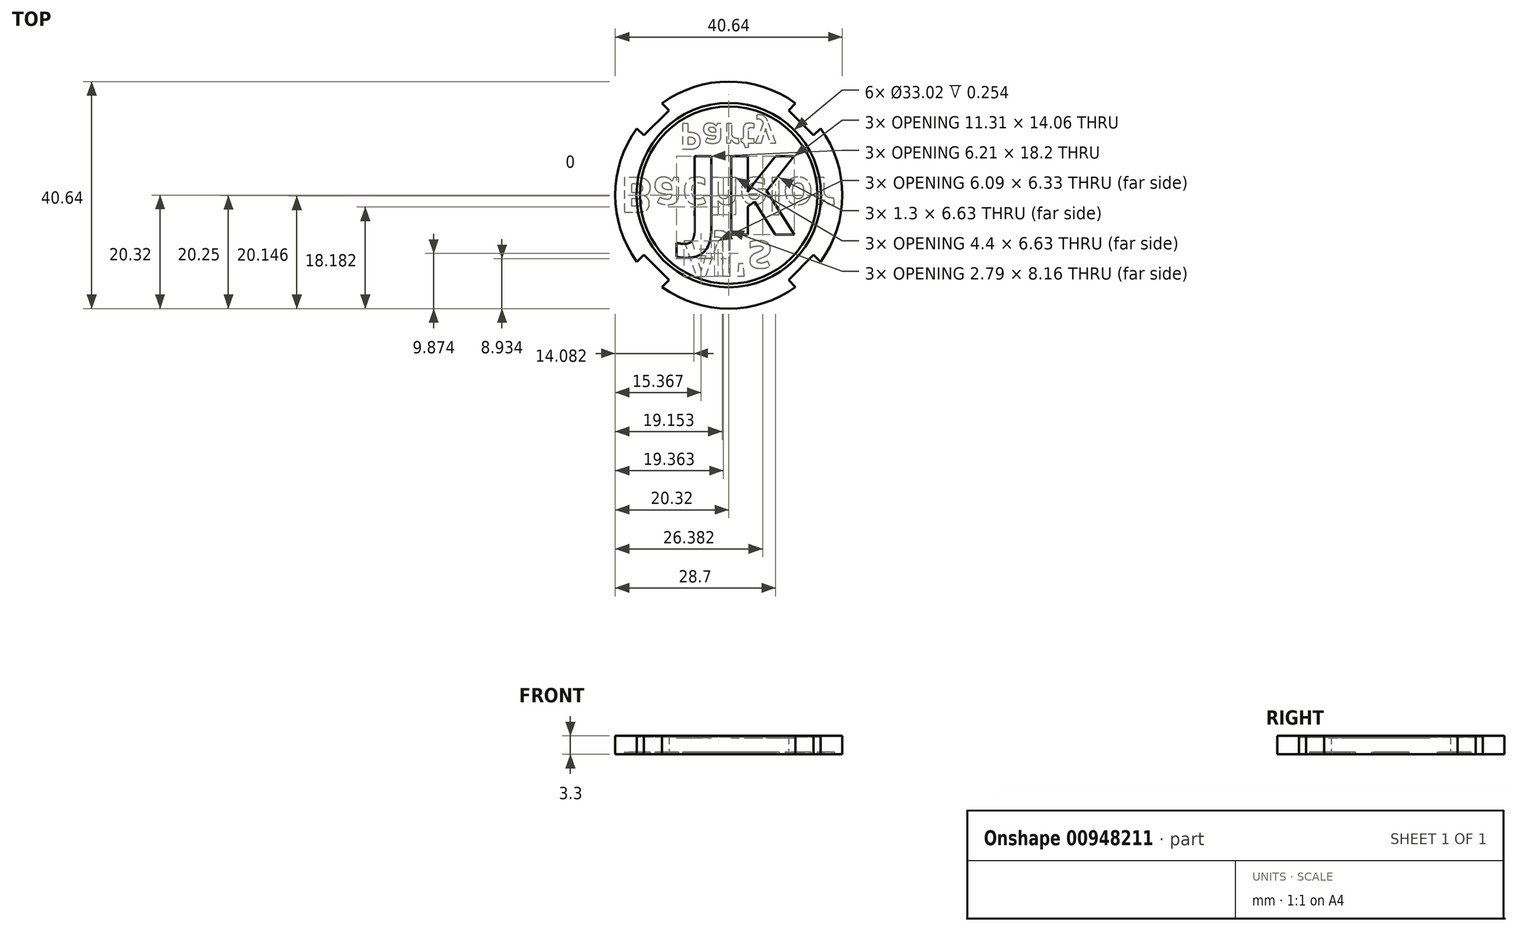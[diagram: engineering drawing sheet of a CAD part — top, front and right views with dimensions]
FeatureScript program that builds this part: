
annotation { "Feature Type Name" : "Feature", "Feature Type Description" : "" }
export const myFeature = defineFeature(function(context is Context, id is Id, definition is map)
    precondition{}
    {
        {
            var Q0;
            Q0=qCreatedBy(makeId("Top.planeOp"),FACE);
            var sketch = newSketch(context, id + "F0", { "sketchPlane" : qUnion([Q0])});
            skCircle(sketch, "E0", {"center": v(0, 0) * mm, "radius": 20.32 * mm});
            skSolve(sketch);
        }
        {
            var Q0;
            Q0=makeQuery(id+"F0.imprint","IMPRINT",FACE,{"disambiguationData":[TD([[makeQuery(id+"F0.imprint","IMPRINT",EDGE,{"derivedFrom":sQuery(id+"F0.wireOp",EDGE,"E0")}),1.0]])]});
            extrude(context, id + "F1", {"entities" : qUnion([Q0]), "depth" : 3.3 * mm, "offsetDistance" : 25.4 * mm});
        }
        {
            var Q0;
            Q0=makeQuery(id+"F1.opExtrude","CAP_FACE",FACE,{"disambiguationData":[OSD([sQuery(id+"F0.wireOp",EDGE,"E0")])],"isStart":true});
            var sketch = newSketch(context, id + "F2", { "sketchPlane" : qUnion([Q0])});
            skText(sketch, "E1", { "text": "Bachelor", "fontName": "OpenSans-Bold.ttf"});
            const initialGuessF2  = {"E1": [-0.01945, -0.00314, 1, 0, 0.00628]};
            skSetInitialGuess(sketch, initialGuessF2);
            skSolve(sketch);
        }
        {
            var Q0;
            Q0=makeQuery(id+"F2.imprint","IMPRINT",FACE,{"disambiguationData":[TD([[makeQuery(id+"F2.imprint","IMPRINT",EDGE,{"derivedFrom":sQuery(id+"F2.wireOp",EDGE,"E1.sketch_text.stroke-0")}),1.0]])]});
            var sketch = newSketch(context, id + "F3", { "sketchPlane" : qUnion([Q0])});
            skText(sketch, "E2", { "text": "AJ\'s", "fontName": "OpenSans-Bold.ttf"});
            const initialGuessF3  = {"E2": [-0.008, 0.00822, 1, 0, 0.00636]};
            skSetInitialGuess(sketch, initialGuessF3);
            skSolve(sketch);
        }
        {
            var Q0;
            Q0=makeQuery(id+"F2.imprint","IMPRINT",FACE,{"disambiguationData":[TD([[makeQuery(id+"F2.imprint","IMPRINT",EDGE,{"derivedFrom":sQuery(id+"F2.wireOp",EDGE,"E1.sketch_text.stroke-0")}),1.0]])]});
            var sketch = newSketch(context, id + "F4", { "sketchPlane" : qUnion([Q0])});
            skText(sketch, "E3", { "text": "Party", "fontName": "OpenSans-Bold.ttf"});
            const initialGuessF4  = {"E3": [-0.00883, -0.01283, 1, 0, 0.00462]};
            skSetInitialGuess(sketch, initialGuessF4);
            skSolve(sketch);
        }
        {
            var Q0;
            Q0=makeQuery(id+"F2.imprint","IMPRINT",FACE,{"disambiguationData":[TD([[makeQuery(id+"F2.imprint","IMPRINT",EDGE,{"derivedFrom":sQuery(id+"F2.wireOp",EDGE,"E1.sketch_text.stroke-0")}),1.0]])]});
            var sketch = newSketch(context, id + "F5", { "sketchPlane" : qUnion([Q0])});
            skLineSegment(sketch, "E4", {"start": v(-14.37, 14.37) * mm, "end": v(14.37, -14.37) * mm, "construction": true});
            skLineSegment(sketch, "E5", {"start": v(-15.18, 10.69) * mm, "end": v(-10.69, 15.18) * mm});
            skLineSegment(sketch, "E6", {"start": v(-10.69, 15.18) * mm, "end": v(-11.95, 16.44) * mm});
            skLineSegment(sketch, "E7", {"start": v(-15.18, 10.69) * mm, "end": v(-16.44, 11.95) * mm});
            skArc(sketch, "E8", {"start": v(-11.95, 16.44) * mm, "mid": v(-14.37, 14.37) * mm, "end": v(-16.44, 11.95) * mm});
            skLineSegment(sketch, "E9.1.0", {"start": v(-15.18, -10.69) * mm, "end": v(-16.44, -11.95) * mm});
            skArc(sketch, "E9.1.1", {"start": v(-16.44, -11.95) * mm, "mid": v(-14.37, -14.37) * mm, "end": v(-11.95, -16.44) * mm});
            skLineSegment(sketch, "E9.1.2", {"start": v(-10.69, -15.18) * mm, "end": v(-11.95, -16.44) * mm});
            skLineSegment(sketch, "E9.1.3", {"start": v(-10.69, -15.18) * mm, "end": v(-15.18, -10.69) * mm});
            skLineSegment(sketch, "E9.2.0", {"start": v(10.69, -15.18) * mm, "end": v(11.95, -16.44) * mm});
            skArc(sketch, "E9.2.1", {"start": v(11.95, -16.44) * mm, "mid": v(14.37, -14.37) * mm, "end": v(16.44, -11.95) * mm});
            skLineSegment(sketch, "E9.2.2", {"start": v(15.18, -10.69) * mm, "end": v(16.44, -11.95) * mm});
            skLineSegment(sketch, "E9.2.3", {"start": v(15.18, -10.69) * mm, "end": v(10.69, -15.18) * mm});
            skLineSegment(sketch, "E9.3.0", {"start": v(15.18, 10.69) * mm, "end": v(16.44, 11.95) * mm});
            skArc(sketch, "E9.3.1", {"start": v(16.44, 11.95) * mm, "mid": v(14.37, 14.37) * mm, "end": v(11.95, 16.44) * mm});
            skLineSegment(sketch, "E9.3.2", {"start": v(10.69, 15.18) * mm, "end": v(11.95, 16.44) * mm});
            skLineSegment(sketch, "E9.3.3", {"start": v(10.69, 15.18) * mm, "end": v(15.18, 10.69) * mm});
            skSolve(sketch);
        }
        {
            var Q0;
            Q0=qSketchRegion(id+"F5",true);
            extrude(context, id + "F6", {"entities" : qUnion([Q0]), "operationType" : NewBodyOperationType.REMOVE, "oppositeDirection" : true, "depth" : 3.3 * mm, "offsetDistance" : 25.4 * mm});
        }
        {
            var Q0;
            Q0=makeQuery(id+"F1.opExtrude","CAP_FACE",FACE,{"disambiguationData":[OSD([sQuery(id+"F0.wireOp",EDGE,"E0")])],"isStart":false});
            var sketch = newSketch(context, id + "F7", { "sketchPlane" : qUnion([Q0])});
            skCircle(sketch, "E10", {"center": v(0, 0) * mm, "radius": 16.51 * mm});
            skCircle(sketch, "E11", {"center": v(0, 0) * mm, "radius": 15.88 * mm});
            skSolve(sketch);
        }
        {
            var Q0;
            Q0=qSketchRegion(id+"F7",true);
            extrude(context, id + "F8", {"entities" : qUnion([Q0]), "operationType" : NewBodyOperationType.REMOVE, "oppositeDirection" : true, "depth" : 0.25 * mm, "offsetDistance" : 25.4 * mm});
        }
        {
            var Q0;
            Q0=qSketchRegion(id+"F2",true);
            extrude(context, id + "F9", {"entities" : qUnion([Q0]), "operationType" : NewBodyOperationType.REMOVE, "oppositeDirection" : true, "depth" : 0.38 * mm, "offsetDistance" : 25.4 * mm});
        }
        {
            var Q0;
            Q0=qSketchRegion(id+"F3",true);
            extrude(context, id + "F10", {"entities" : qUnion([Q0]), "operationType" : NewBodyOperationType.REMOVE, "oppositeDirection" : true, "depth" : 0.38 * mm, "offsetDistance" : 25.4 * mm});
        }
        {
            var Q0;
            Q0=qSketchRegion(id+"F4",true);
            extrude(context, id + "F11", {"entities" : qUnion([Q0]), "operationType" : NewBodyOperationType.REMOVE, "oppositeDirection" : true, "depth" : 0.38 * mm, "offsetDistance" : 25.4 * mm});
        }
        {
            var Q0;
            Q0=makeQuery(id+"F8.boolean.opBoolean","SPLIT",FACE,{"disambiguationData":[TD([makeQuery(id+"F8.opExtrude","SWEPT_FACE",FACE,{"disambiguationData":[OSD([sQuery(id+"F7.wireOp",EDGE,"E11")])]})])],"derivedFrom":makeQuery(id+"F1.opExtrude","CAP_FACE",FACE,{"disambiguationData":[OSD([sQuery(id+"F0.wireOp",EDGE,"E0")])],"isStart":false})});
            var sketch = newSketch(context, id + "F12", { "sketchPlane" : qUnion([Q0])});
            skText(sketch, "E12", { "text": " JK", "fontName": "OpenSans-Bold.ttf"});
            const initialGuessF12  = {"E12": [-0.013, -0.0071, 1, 0, 0.01418]};
            skSetInitialGuess(sketch, initialGuessF12);
            skSolve(sketch);
        }
        {
            var Q0;
            Q0=qSketchRegion(id+"F12",true);
            extrude(context, id + "F13", {"entities" : qUnion([Q0]), "operationType" : NewBodyOperationType.REMOVE, "oppositeDirection" : true, "depth" : 0.38 * mm, "offsetDistance" : 25.4 * mm});
        }
    });
